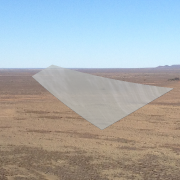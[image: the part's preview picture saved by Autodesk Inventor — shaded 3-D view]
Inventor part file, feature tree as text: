
AUTODESK INVENTOR PART (.ipt)
format: ipt  version: 2013 SP2 (Build 170200200, 200)  size: 152,064 bytes
history: native  units: in
note: dims shown in document units (in); Inventor stores cm internally (conversion verified against a paired STEP export)
features: sketch x3, sweep x1, extrude x1, other x1
ambient origin geometry x8: Origin, YZ Plane, XZ Plane, XY Plane, X Axis, Y Axis, Z Axis, Center Point
bodies: Solid1 (feature_tree)
feature tree (6):
  sweep  "Sweep1"
  extrude  "Extrusion1"  TaperAngle=0.0deg  [1 undecoded]
  sketch  "Sketch1"  dims[d0=0.0in d1=100.0in d2=48.0in]
  other  "2D Equation Curve1"
  sketch  "Sketch2"  dims[d4=0.25in d5=0.0in]
  sketch  "Sketch3"  dims[d6=2.0in d10=18.0in d11=100.0in d12=165.0deg d13=100.0in d14=0.0in]
note: 1 required parameter value undecoded (feature->parameter linkage not recoverable at this tier; creation-order binding heuristic only, values carry confidence <= 0.55)
